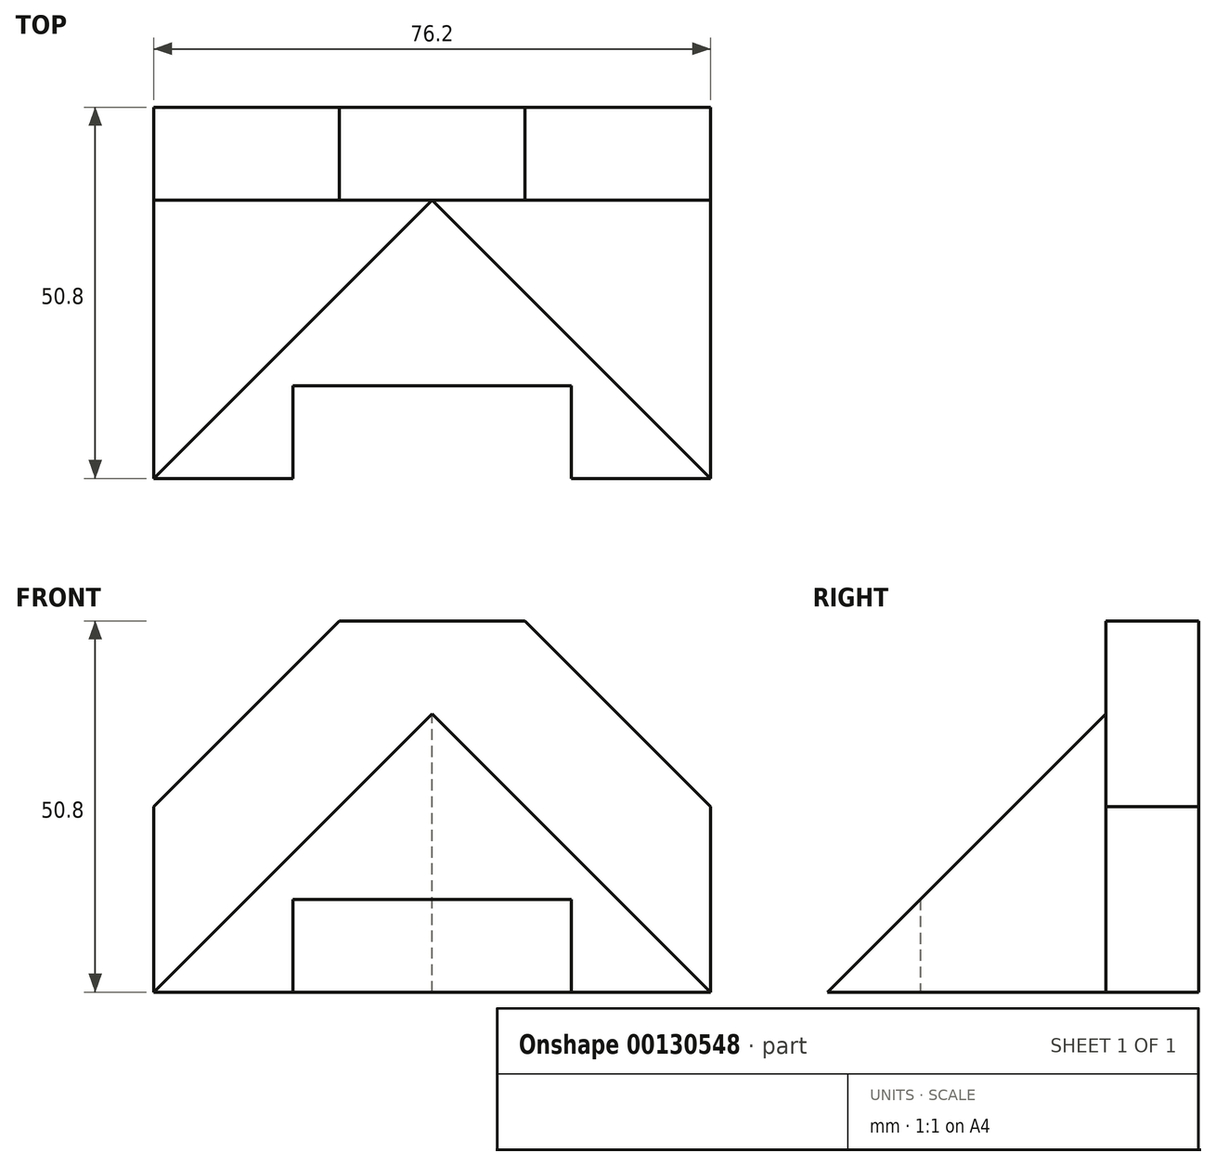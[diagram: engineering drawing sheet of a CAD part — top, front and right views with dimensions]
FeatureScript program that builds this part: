
annotation { "Feature Type Name" : "Feature", "Feature Type Description" : "" }
export const myFeature = defineFeature(function(context is Context, id is Id, definition is map)
    precondition{}
    {
        {
            var Q0;
            Q0=qCreatedBy(makeId("Front.planeOp"),FACE);
            var sketch = newSketch(context, id + "F0", { "sketchPlane" : qUnion([Q0])});
            skLineSegment(sketch, "E0", {"start": v(0, 0) * mm, "end": v(76.2, 0) * mm});
            skLineSegment(sketch, "E1", {"start": v(76.2, 0) * mm, "end": v(76.2, 25.4) * mm});
            skLineSegment(sketch, "E2", {"start": v(76.2, 25.4) * mm, "end": v(50.8, 50.8) * mm});
            skLineSegment(sketch, "E3", {"start": v(50.8, 50.8) * mm, "end": v(25.4, 50.8) * mm});
            skLineSegment(sketch, "E4", {"start": v(25.4, 50.8) * mm, "end": v(0, 25.4) * mm});
            skLineSegment(sketch, "E5", {"start": v(0, 25.4) * mm, "end": v(0, 0) * mm});
            skLineSegment(sketch, "E6", {"start": v(0, 0) * mm, "end": v(38.1, 38.1) * mm});
            skLineSegment(sketch, "E7", {"start": v(38.1, 38.1) * mm, "end": v(76.2, 0) * mm});
            skLineSegment(sketch, "E8", {"start": v(57.15, 0) * mm, "end": v(57.15, 12.7) * mm});
            skLineSegment(sketch, "E9", {"start": v(57.15, 12.7) * mm, "end": v(19.05, 12.7) * mm});
            skLineSegment(sketch, "E10", {"start": v(19.05, 12.7) * mm, "end": v(19.05, 0) * mm});
            skLineSegment(sketch, "E11", {"start": v(0, 25.4) * mm, "end": v(0, 50.8) * mm});
            skLineSegment(sketch, "E12", {"start": v(0, 50.8) * mm, "end": v(25.4, 50.8) * mm});
            skLineSegment(sketch, "E13", {"start": v(50.8, 50.8) * mm, "end": v(76.2, 50.8) * mm});
            skLineSegment(sketch, "E14", {"start": v(76.2, 50.8) * mm, "end": v(76.2, 25.4) * mm});
            skSolve(sketch);
        }
        {
            var Q0;
            Q0=qCreatedBy(makeId("Top.planeOp"),FACE);
            var sketch = newSketch(context, id + "F1", { "sketchPlane" : qUnion([Q0])});
            skLineSegment(sketch, "E15", {"start": v(0, 0) * mm, "end": v(0, 50.8) * mm});
            skLineSegment(sketch, "E16", {"start": v(0, 50.8) * mm, "end": v(76.2, 50.8) * mm});
            skLineSegment(sketch, "E17", {"start": v(76.2, 50.8) * mm, "end": v(76.2, 0) * mm});
            skLineSegment(sketch, "E18", {"start": v(76.2, 0) * mm, "end": v(57.15, 0) * mm});
            skLineSegment(sketch, "E19", {"start": v(57.15, 0) * mm, "end": v(57.15, 12.7) * mm});
            skLineSegment(sketch, "E20", {"start": v(57.15, 12.7) * mm, "end": v(19.05, 12.7) * mm});
            skLineSegment(sketch, "E21", {"start": v(19.05, 12.7) * mm, "end": v(19.05, 0) * mm});
            skLineSegment(sketch, "E22", {"start": v(19.05, 0) * mm, "end": v(0, 0) * mm});
            skLineSegment(sketch, "E23", {"start": v(0, 38.1) * mm, "end": v(76.2, 38.1) * mm});
            skLineSegment(sketch, "E24", {"start": v(50.8, 38.1) * mm, "end": v(50.8, 50.8) * mm});
            skLineSegment(sketch, "E25", {"start": v(25.4, 50.8) * mm, "end": v(25.4, 38.1) * mm});
            skLineSegment(sketch, "E26", {"start": v(19.05, 0) * mm, "end": v(57.15, 0) * mm});
            skSolve(sketch);
        }
        {
            var Q0;
            Q0=qCreatedBy(makeId("Right.planeOp"),FACE);
            var sketch = newSketch(context, id + "F2", { "sketchPlane" : qUnion([Q0])});
            skLineSegment(sketch, "E27", {"start": v(0, 0) * mm, "end": v(50.8, 0) * mm});
            skLineSegment(sketch, "E28", {"start": v(50.8, 0) * mm, "end": v(50.8, 50.8) * mm});
            skLineSegment(sketch, "E29", {"start": v(50.8, 50.8) * mm, "end": v(38.1, 50.8) * mm});
            skLineSegment(sketch, "E30", {"start": v(38.1, 50.8) * mm, "end": v(38.1, 0) * mm});
            skLineSegment(sketch, "E31", {"start": v(38.1, 25.4) * mm, "end": v(50.8, 25.4) * mm});
            skLineSegment(sketch, "E32", {"start": v(38.1, 38.1) * mm, "end": v(0, 0) * mm});
            skSolve(sketch);
        }
        {
            var Q0;
            {var subQ1=sQuery(id+"F2.wireOp",EDGE,"E29");Q0=makeQuery(id+"F2.imprint","IMPRINT",FACE,{"disambiguationData":[TD([[makeQuery(id+"F2.imprint","IMPRINT",EDGE,{"derivedFrom":subQ1}),1.0]])]});}
            var Q1;
            {var subQ5=sQuery(id+"F2.wireOp",EDGE,"E31");Q1=makeQuery(id+"F2.imprint","IMPRINT",FACE,{"disambiguationData":[TD([[makeQuery(id+"F2.imprint","IMPRINT",EDGE,{"derivedFrom":subQ5}),-1.0]])]});}
            extrude(context, id + "F3", {"entities" : qUnion([Q0, Q1]), "depth" : 76.2 * mm});
        }
        {
            var Q0;
            Q0=makeQuery(id+"F0.imprint","IMPRINT",FACE,{"disambiguationData":[TD([[makeQuery(id+"F0.imprint","IMPRINT",EDGE,{"derivedFrom":sQuery(id+"F0.wireOp",EDGE,"E4")}),-1.0]])]});
            var Q1;
            Q1=makeQuery(id+"F0.imprint","IMPRINT",FACE,{"disambiguationData":[TD([[makeQuery(id+"F0.imprint","IMPRINT",EDGE,{"derivedFrom":sQuery(id+"F0.wireOp",EDGE,"E2")}),-1.0]])]});
            extrude(context, id + "F4", {"entities" : qUnion([Q0, Q1]), "operationType" : NewBodyOperationType.REMOVE, "endBound" : BoundingType.THROUGH_ALL, "oppositeDirection" : true, "depth" : 25.4 * mm});
        }
        {
            var Q0;
            Q0=makeQuery(id+"F3.opExtrude","SWEPT_FACE",FACE,{"disambiguationData":[OSD([sQuery(id+"F2.wireOp",EDGE,"E29")])]});
            var sketch = newSketch(context, id + "F5", { "sketchPlane" : qUnion([Q0])});
            skLineSegment(sketch, "E33", {"start": v(38.1, 38.1) * mm, "end": v(76.2, 0) * mm});
            skLineSegment(sketch, "E34", {"start": v(76.2, 0) * mm, "end": v(0, 0) * mm});
            skLineSegment(sketch, "E35", {"start": v(0, 0) * mm, "end": v(38.1, 38.1) * mm});
            skSolve(sketch);
        }
        {
            var Q0;
            Q0=makeQuery(id+"F5.imprint","IMPRINT",FACE,{"disambiguationData":[TD([[makeQuery(id+"F5.imprint","IMPRINT",EDGE,{"derivedFrom":sQuery(id+"F5.wireOp",EDGE,"E33")}),-1.0]])]});
            extrude(context, id + "F6", {"entities" : qUnion([Q0]), "oppositeDirection" : true, "depth" : 50.8 * mm});
        }
        {
            var Q0;
            Q0=makeQuery(id+"F0.imprint","IMPRINT",FACE,{"disambiguationData":[TD([[makeQuery(id+"F0.imprint","IMPRINT",EDGE,{"derivedFrom":sQuery(id+"F0.wireOp",EDGE,"E1")}),1.0]])]});
            var Q1;
            Q1=makeQuery(id+"F3.opExtrude","SWEPT_FACE",FACE,{"disambiguationData":[OSD([sQuery(id+"F2.wireOp",EDGE,"E30")])]});
            extrude(context, id + "F7", {"entities" : qUnion([Q0]), "operationType" : NewBodyOperationType.REMOVE, "endBound" : BoundingType.UP_TO_SURFACE, "oppositeDirection" : true, "endBoundEntityFace" : qUnion([Q1]), "depth" : 25.4 * mm});
        }
        {
            var Q0;
            {var subQ0=sQuery(id+"F2.wireOp",EDGE,"E32");Q0=makeQuery(id+"F2.imprint","IMPRINT",FACE,{"disambiguationData":[TD([[makeQuery(id+"F2.imprint","IMPRINT",EDGE,{"derivedFrom":subQ0}),1.0]])]});}
            extrude(context, id + "F8", {"entities" : qUnion([Q0]), "depth" : 76.2 * mm});
        }
        {
            var Q0;
            {var subQ1=sQuery(id+"F5.wireOp",EDGE,"E34");Q0=makeQuery(id+"F7.boolean.opBoolean","SPLIT",FACE,{"disambiguationData":[TD([makeQuery(id+"F7.opExtrude","SWEPT_FACE",FACE,{"disambiguationData":[OSD([sQuery(id+"F0.wireOp",EDGE,"E2")])]})])],"derivedFrom":makeQuery(id+"F6.opExtrude","SWEPT_FACE",FACE,{"disambiguationData":[OSD([subQ1])]})});}
            var Q1;
            {var subQ1=sQuery(id+"F5.wireOp",EDGE,"E34");Q1=makeQuery(id+"F7.boolean.opBoolean","SPLIT",FACE,{"disambiguationData":[TD([makeQuery(id+"F7.opExtrude","SWEPT_FACE",FACE,{"disambiguationData":[OSD([sQuery(id+"F0.wireOp",EDGE,"E4")])]})])],"derivedFrom":makeQuery(id+"F6.opExtrude","SWEPT_FACE",FACE,{"disambiguationData":[OSD([subQ1])]})});}
            extrude(context, id + "F9", {"entities" : qUnion([Q0, Q1]), "operationType" : NewBodyOperationType.REMOVE, "endBound" : BoundingType.THROUGH_ALL, "oppositeDirection" : true, "depth" : 25.4 * mm});
        }
        {
            var Q0;
            Q0=makeQuery(id+"F8.opExtrude","SWEPT_FACE",FACE,{"disambiguationData":[OSD([sQuery(id+"F2.wireOp",EDGE,"E32")])]});
            var sketch = newSketch(context, id + "F10", { "sketchPlane" : qUnion([Q0])});
            skSolve(sketch);
        }
        {
            var Q0;
            {var subQ0=sQuery(id+"F2.wireOp",EDGE,"E32");Q0=makeQuery(id+"F10.imprint","IMPRINT",FACE,{"disambiguationData":[TD([[makeQuery(id+"F10.imprint","IMPRINT",EDGE,{"derivedFrom":makeQuery(id+"F8.opExtrude","CAP_EDGE",EDGE,{"disambiguationData":[OSD([subQ0])],"isStart":true})}),1.0]])]});}
            var Q1;
            Q1=makeQuery(id+"F7.boolean.opBoolean","COPY",FACE,{"derivedFrom":makeQuery(id+"F7.opExtrude","SWEPT_FACE",FACE,{"disambiguationData":[OSD([sQuery(id+"F0.wireOp",EDGE,"E7")])]})});
            extrude(context, id + "F11", {"entities" : qUnion([Q0]), "operationType" : NewBodyOperationType.REMOVE, "endBound" : BoundingType.UP_TO_SURFACE, "endBoundEntityFace" : qUnion([Q1]), "depth" : 25.4 * mm});
        }
        {
            var Q0;
            Q0=makeQuery(id+"F3.opExtrude","SWEPT_FACE",FACE,{"disambiguationData":[OSD([sQuery(id+"F2.wireOp",EDGE,"E30")])]});
            var sketch = newSketch(context, id + "F12", { "sketchPlane" : qUnion([Q0])});
            skLineSegment(sketch, "E36", {"start": v(38.1, 38.1) * mm, "end": v(76.2, 0) * mm});
            skLineSegment(sketch, "E37", {"start": v(76.2, 0) * mm, "end": v(76.2, 38.1) * mm});
            skLineSegment(sketch, "E38", {"start": v(76.2, 38.1) * mm, "end": v(38.1, 38.1) * mm});
            skLineSegment(sketch, "E39", {"start": v(38.1, 38.1) * mm, "end": v(38.1, -16.34) * mm, "construction": true});
            skPoint(sketch, "E39.endSnap0", {"position": v(38.1, 0) * mm});
            skLineSegment(sketch, "E40.MirrorCS", {"start": v(0, 38.1) * mm, "end": v(38.1, 38.1) * mm});
            skLineSegment(sketch, "E41.MirrorCS", {"start": v(0, 0) * mm, "end": v(0, 38.1) * mm});
            skLineSegment(sketch, "E42.MirrorCS", {"start": v(38.1, 38.1) * mm, "end": v(0, 0) * mm});
            skLineSegment(sketch, "E43", {"start": v(0, 0) * mm, "end": v(38.1, 38.1) * mm});
            skSolve(sketch);
        }
        {
            var Q0;
            Q0 = qSketchRegion(id + "F12", true);
            var Q1;
            {var subQ2=sQuery(id+"F5.wireOp",EDGE,"E34");Q1=makeQuery(id+"F7.boolean.opBoolean","SPLIT",FACE,{"disambiguationData":[TD([makeQuery(id+"F7.opExtrude","SWEPT_FACE",FACE,{"disambiguationData":[OSD([sQuery(id+"F0.wireOp",EDGE,"E6")])]})])],"derivedFrom":makeQuery(id+"F6.opExtrude","SWEPT_FACE",FACE,{"disambiguationData":[OSD([subQ2])]})});}
            extrude(context, id + "F13", {"entities" : qUnion([Q0]), "operationType" : NewBodyOperationType.REMOVE, "endBoundEntityFace" : qUnion([Q1]), "depth" : 76.2 * mm});
        }
        {
            var Q0;
            Q0=makeQuery(id+"F1.imprint","IMPRINT",FACE,{"disambiguationData":[TD([[makeQuery(id+"F1.imprint","IMPRINT",EDGE,{"derivedFrom":sQuery(id+"F1.wireOp",EDGE,"E19")}),1.0]])]});
            extrude(context, id + "F14", {"entities" : qUnion([Q0]), "operationType" : NewBodyOperationType.REMOVE, "depth" : 12.7 * mm});
        }
    });
